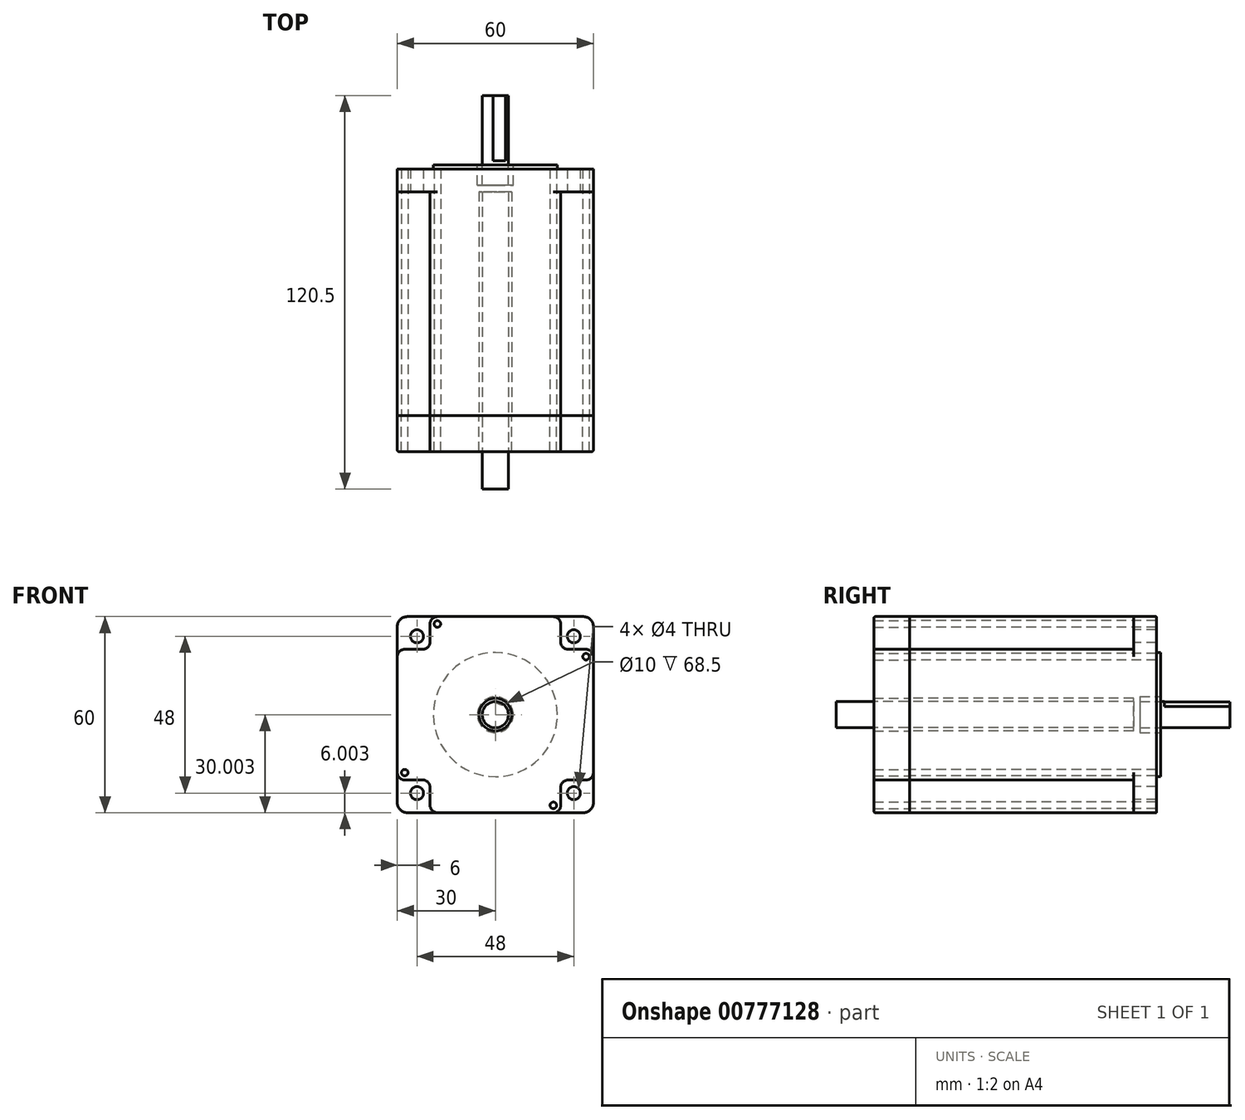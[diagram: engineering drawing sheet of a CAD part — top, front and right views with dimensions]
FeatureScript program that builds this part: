
annotation { "Feature Type Name" : "Feature", "Feature Type Description" : "" }
export const myFeature = defineFeature(function(context is Context, id is Id, definition is map)
    precondition{}
    {
        {
            var Q0;
            Q0=qCreatedBy(makeId("Front.planeOp"),FACE);
            var sketch = newSketch(context, id + "F0", { "sketchPlane" : qUnion([Q0])});
            skLineSegment(sketch, "E0.bottom", {"start": v(-39, 29.62) * mm, "end": v(-3.5, 29.62) * mm});
            skLineSegment(sketch, "E0.top", {"start": v(-39, -30.38) * mm, "end": v(-3.5, -30.38) * mm});
            skLineSegment(sketch, "E0.left", {"start": v(-51.25, 17.37) * mm, "end": v(-51.25, -18.13) * mm});
            skLineSegment(sketch, "E0.right", {"start": v(8.75, 17.37) * mm, "end": v(8.75, -18.13) * mm});
            skLineSegment(sketch, "E1.bottom", {"start": v(-49, 29.62) * mm, "end": v(-41.25, 29.62) * mm});
            skLineSegment(sketch, "E1.top", {"start": v(-49, 19.62) * mm, "end": v(-43.5, 19.62) * mm});
            skLineSegment(sketch, "E1.left", {"start": v(-51.25, 27.37) * mm, "end": v(-51.25, 19.62) * mm});
            skLineSegment(sketch, "E1.right", {"start": v(-41.25, 27.37) * mm, "end": v(-41.25, 21.87) * mm});
            skLineSegment(sketch, "E2.bottom", {"start": v(6.5, 19.62) * mm, "end": v(1, 19.62) * mm});
            skLineSegment(sketch, "E2.top", {"start": v(6.5, 29.62) * mm, "end": v(0, 29.62) * mm});
            skLineSegment(sketch, "E2.left", {"start": v(8.75, 19.62) * mm, "end": v(8.75, 27.37) * mm});
            skLineSegment(sketch, "E2.right", {"start": v(-1.25, 21.87) * mm, "end": v(-1.25, 27.37) * mm});
            skLineSegment(sketch, "E3.bottom", {"start": v(-43.5, -20.38) * mm, "end": v(-49, -20.38) * mm});
            skLineSegment(sketch, "E3.top", {"start": v(-41.25, -30.38) * mm, "end": v(-49, -30.38) * mm});
            skLineSegment(sketch, "E3.left", {"start": v(-41.25, -22.63) * mm, "end": v(-41.25, -28.13) * mm});
            skLineSegment(sketch, "E3.right", {"start": v(-51.25, -20.38) * mm, "end": v(-51.25, -28.13) * mm});
            skLineSegment(sketch, "E4.bottom", {"start": v(1, -20.38) * mm, "end": v(6.5, -20.38) * mm});
            skLineSegment(sketch, "E4.top", {"start": v(-1.25, -30.38) * mm, "end": v(6.5, -30.38) * mm});
            skLineSegment(sketch, "E4.left", {"start": v(-1.25, -22.63) * mm, "end": v(-1.25, -28.13) * mm});
            skLineSegment(sketch, "E4.right", {"start": v(8.75, -20.38) * mm, "end": v(8.75, -28.13) * mm});
            skArc(sketch, "E5.filletArc", {"start": v(-1.25, 27.37) * mm, "mid": v(-1.9, 28.96) * mm, "end": v(-3.5, 29.62) * mm});
            skPoint(sketch, "E6.visualSharp", {"position": v(-1.25, 19.62) * mm});
            skArc(sketch, "E6.filletArc", {"start": v(-1.25, 21.87) * mm, "mid": v(-0.6, 20.28) * mm, "end": v(1, 19.62) * mm});
            skPoint(sketch, "E7.newPointA", {"position": v(8.75, 19.62) * mm});
            skArc(sketch, "E7.filletArc", {"start": v(8.75, 17.37) * mm, "mid": v(8.1, 18.96) * mm, "end": v(6.5, 19.62) * mm});
            skPoint(sketch, "E8.visualSharp", {"position": v(-1.25, -20.38) * mm});
            skArc(sketch, "E8.filletArc", {"start": v(1, -20.38) * mm, "mid": v(-0.6, -21.04) * mm, "end": v(-1.25, -22.63) * mm});
            skArc(sketch, "E9.filletArc", {"start": v(6.5, -20.38) * mm, "mid": v(8.1, -19.72) * mm, "end": v(8.75, -18.13) * mm});
            skArc(sketch, "E10.filletArc", {"start": v(-3.5, -30.38) * mm, "mid": v(-1.9, -29.72) * mm, "end": v(-1.25, -28.13) * mm});
            skArc(sketch, "E11.filletArc", {"start": v(-41.25, -28.13) * mm, "mid": v(-40.6, -29.72) * mm, "end": v(-39, -30.38) * mm});
            skPoint(sketch, "E12.visualSharp", {"position": v(-41.25, -20.38) * mm});
            skArc(sketch, "E12.filletArc", {"start": v(-41.25, -22.63) * mm, "mid": v(-41.9, -21.04) * mm, "end": v(-43.5, -20.38) * mm});
            skPoint(sketch, "E13.newPointA", {"position": v(-51.25, -30.38) * mm});
            skArc(sketch, "E13.filletArc", {"start": v(-51.25, -18.13) * mm, "mid": v(-50.6, -19.72) * mm, "end": v(-49, -20.38) * mm});
            skPoint(sketch, "E14.newPointA", {"position": v(-51.25, 19.62) * mm});
            skPoint(sketch, "E14.newPointB", {"position": v(-51.25, 29.62) * mm});
            skArc(sketch, "E14.filletArc", {"start": v(-49, 19.62) * mm, "mid": v(-50.6, 18.96) * mm, "end": v(-51.25, 17.37) * mm});
            skPoint(sketch, "E15.visualSharp", {"position": v(-41.25, 19.62) * mm});
            skArc(sketch, "E15.filletArc", {"start": v(-43.5, 19.62) * mm, "mid": v(-41.9, 20.28) * mm, "end": v(-41.25, 21.87) * mm});
            skPoint(sketch, "E16.newPointB", {"position": v(-41.25, 29.62) * mm});
            skArc(sketch, "E16.filletArc", {"start": v(-39, 29.62) * mm, "mid": v(-40.6, 28.96) * mm, "end": v(-41.25, 27.37) * mm});
            skArc(sketch, "E17.filletArc", {"start": v(-49, 29.62) * mm, "mid": v(-50.6, 28.96) * mm, "end": v(-51.25, 27.37) * mm});
            skPoint(sketch, "E18.visualSharp", {"position": v(8.75, 29.62) * mm});
            skArc(sketch, "E18.filletArc", {"start": v(8.75, 27.37) * mm, "mid": v(8.1, 28.96) * mm, "end": v(6.5, 29.62) * mm});
            skPoint(sketch, "E19.visualSharp", {"position": v(8.75, -30.38) * mm});
            skArc(sketch, "E19.filletArc", {"start": v(6.5, -30.38) * mm, "mid": v(8.1, -29.72) * mm, "end": v(8.75, -28.13) * mm});
            skArc(sketch, "E20.filletArc", {"start": v(-51.25, -28.13) * mm, "mid": v(-50.6, -29.72) * mm, "end": v(-49, -30.38) * mm});
            skLineSegment(sketch, "E21", {"start": v(-51.25, 19.62) * mm, "end": v(-51.25, 17.37) * mm});
            skLineSegment(sketch, "E22", {"start": v(-51.25, -18.13) * mm, "end": v(-51.25, -20.38) * mm});
            skLineSegment(sketch, "E23", {"start": v(-41.25, -30.38) * mm, "end": v(-39, -30.38) * mm});
            skLineSegment(sketch, "E24", {"start": v(-3.6, -30.34) * mm, "end": v(-1.25, -30.38) * mm});
            skLineSegment(sketch, "E25", {"start": v(8.75, -20.38) * mm, "end": v(8.75, -18.13) * mm});
            skLineSegment(sketch, "E26", {"start": v(8.75, 17.37) * mm, "end": v(8.75, 19.62) * mm});
            skLineSegment(sketch, "E27", {"start": v(0, 29.62) * mm, "end": v(-3.5, 29.62) * mm});
            skLineSegment(sketch, "E28", {"start": v(-39, 29.62) * mm, "end": v(-41.25, 29.62) * mm});
            skCircle(sketch, "E29", {"center": v(-39, 27.37) * mm, "radius": 1 * mm});
            skCircle(sketch, "E30", {"center": v(6.5, 17.37) * mm, "radius": 1 * mm});
            skCircle(sketch, "E31", {"center": v(-3.5, -28.13) * mm, "radius": 1 * mm});
            skCircle(sketch, "E32", {"center": v(-49, -18.13) * mm, "radius": 1 * mm});
            skCircle(sketch, "E33", {"center": v(-21.25, -0.38) * mm, "radius": 5 * mm});
            skPoint(sketch, "E33.centerSnap0", {"position": v(-21.25, 29.62) * mm});
            skPoint(sketch, "E33.centerSnap1", {"position": v(-51.25, -0.38) * mm});
            skCircle(sketch, "E34", {"center": v(-21.25, -0.38) * mm, "radius": 4 * mm});
            skSolve(sketch);
        }
        {
            var Q0;
            Q0=makeQuery(id+"F0.imprint","IMPRINT",FACE,{"disambiguationData":[TD([[makeQuery(id+"F0.imprint","IMPRINT",EDGE,{"derivedFrom":sQuery(id+"F0.wireOp",EDGE,"E0.bottom")}),-1.0]])]});
            extrude(context, id + "F1", {"entities" : qUnion([Q0]), "depth" : 11 * mm, "offsetDistance" : 25 * mm});
        }
        {
            var Q0;
            Q0=makeQuery(id+"F1.opExtrude","CAP_EDGE",EDGE,{"disambiguationData":[OSD([sQuery(id+"F0.wireOp",EDGE,"E0.left")])],"isStart":false});
            fillet(context, id + "F2", {"entities" : qUnion([Q0]), "radius" : .5 * mm, "tangentPropagation" : true, "allowEdgeOverflow" : false});
        }
        {
            var Q0;
            Q0=makeQuery(id+"F1.opExtrude","CAP_FACE",FACE,{"disambiguationData":[OSD([sQuery(id+"F0.wireOp",EDGE,"E0.bottom"),sQuery(id+"F0.wireOp",EDGE,"E0.top"),sQuery(id+"F0.wireOp",EDGE,"E0.left"),sQuery(id+"F0.wireOp",EDGE,"E0.right"),sQuery(id+"F0.wireOp",EDGE,"E1.top"),sQuery(id+"F0.wireOp",EDGE,"E1.right"),sQuery(id+"F0.wireOp",EDGE,"E2.bottom"),sQuery(id+"F0.wireOp",EDGE,"E2.right"),sQuery(id+"F0.wireOp",EDGE,"E3.bottom"),sQuery(id+"F0.wireOp",EDGE,"E3.left"),sQuery(id+"F0.wireOp",EDGE,"E4.bottom"),sQuery(id+"F0.wireOp",EDGE,"E4.left"),sQuery(id+"F0.wireOp",EDGE,"E5.filletArc"),sQuery(id+"F0.wireOp",EDGE,"E6.filletArc"),sQuery(id+"F0.wireOp",EDGE,"E7.filletArc"),sQuery(id+"F0.wireOp",EDGE,"E8.filletArc"),sQuery(id+"F0.wireOp",EDGE,"E9.filletArc"),sQuery(id+"F0.wireOp",EDGE,"E10.filletArc"),sQuery(id+"F0.wireOp",EDGE,"E11.filletArc"),sQuery(id+"F0.wireOp",EDGE,"E12.filletArc"),sQuery(id+"F0.wireOp",EDGE,"E13.filletArc"),sQuery(id+"F0.wireOp",EDGE,"E14.filletArc"),sQuery(id+"F0.wireOp",EDGE,"E15.filletArc"),sQuery(id+"F0.wireOp",EDGE,"E16.filletArc"),sQuery(id+"F0.wireOp",EDGE,"E29"),sQuery(id+"F0.wireOp",EDGE,"E30"),sQuery(id+"F0.wireOp",EDGE,"E31"),sQuery(id+"F0.wireOp",EDGE,"E32"),sQuery(id+"F0.wireOp",EDGE,"E33")])],"isStart":true});
            var sketch = newSketch(context, id + "F3", { "sketchPlane" : qUnion([Q0])});
            skSolve(sketch);
        }
        {
            var Q0;
            Q0 = qSketchRegion(id + "F3", true);
            var Q1;
            Q1=makeQuery(id+"F3.imprint","IMPRINT",FACE,{"disambiguationData":[TD([[makeQuery(id+"F3.imprint","IMPRINT",EDGE,{"derivedFrom":makeQuery(id+"F1.opExtrude","CAP_EDGE",EDGE,{"disambiguationData":[OSD([sQuery(id+"F0.wireOp",EDGE,"E0.bottom")])],"isStart":true})}),1.0]])]});
            extrude(context, id + "F4", {"entities" : qUnion([Q0, Q1]), "depth" : 65.5 * mm, "offsetDistance" : 25 * mm});
        }
        {
            var Q0;
            Q0=makeQuery(id+"F4.opExtrude","SWEPT_FACE",FACE,{"disambiguationData":[OSD([sQuery(id+"F0.wireOp",EDGE,"E1.right")])]});
            var sketch = newSketch(context, id + "F5", { "sketchPlane" : qUnion([Q0])});
            skSolve(sketch);
        }
        {
            var Q0;
            Q0 = qSketchRegion(id + "F5", true);
            var Q1;
            Q1=makeQuery(id+"F4.opExtrude","CAP_FACE",FACE,{"disambiguationData":[OSD([sQuery(id+"F0.wireOp",EDGE,"E0.bottom"),sQuery(id+"F0.wireOp",EDGE,"E0.top"),sQuery(id+"F0.wireOp",EDGE,"E0.left"),sQuery(id+"F0.wireOp",EDGE,"E0.right"),sQuery(id+"F0.wireOp",EDGE,"E1.top"),sQuery(id+"F0.wireOp",EDGE,"E1.right"),sQuery(id+"F0.wireOp",EDGE,"E2.bottom"),sQuery(id+"F0.wireOp",EDGE,"E2.right"),sQuery(id+"F0.wireOp",EDGE,"E3.bottom"),sQuery(id+"F0.wireOp",EDGE,"E3.left"),sQuery(id+"F0.wireOp",EDGE,"E4.bottom"),sQuery(id+"F0.wireOp",EDGE,"E4.left"),sQuery(id+"F0.wireOp",EDGE,"E5.filletArc"),sQuery(id+"F0.wireOp",EDGE,"E6.filletArc"),sQuery(id+"F0.wireOp",EDGE,"E7.filletArc"),sQuery(id+"F0.wireOp",EDGE,"E8.filletArc"),sQuery(id+"F0.wireOp",EDGE,"E9.filletArc"),sQuery(id+"F0.wireOp",EDGE,"E10.filletArc"),sQuery(id+"F0.wireOp",EDGE,"E11.filletArc"),sQuery(id+"F0.wireOp",EDGE,"E12.filletArc"),sQuery(id+"F0.wireOp",EDGE,"E13.filletArc"),sQuery(id+"F0.wireOp",EDGE,"E14.filletArc"),sQuery(id+"F0.wireOp",EDGE,"E15.filletArc"),sQuery(id+"F0.wireOp",EDGE,"E16.filletArc"),sQuery(id+"F0.wireOp",EDGE,"E29"),sQuery(id+"F0.wireOp",EDGE,"E30"),sQuery(id+"F0.wireOp",EDGE,"E31"),sQuery(id+"F0.wireOp",EDGE,"E32"),sQuery(id+"F0.wireOp",EDGE,"E33")])],"isStart":false});
            extrude(context, id + "F6", {"entities" : qUnion([Q0, Q1]), "operationType" : NewBodyOperationType.ADD, "depth" : 3 * mm, "offsetDistance" : 25 * mm});
        }
        {
            var Q0;
            Q0=makeQuery(id+"F6.opExtrude","CAP_FACE",FACE,{"disambiguationData":[OSD([sQuery(id+"F0.wireOp",EDGE,"E0.bottom"),sQuery(id+"F0.wireOp",EDGE,"E0.top"),sQuery(id+"F0.wireOp",EDGE,"E0.left"),sQuery(id+"F0.wireOp",EDGE,"E0.right"),sQuery(id+"F0.wireOp",EDGE,"E1.top"),sQuery(id+"F0.wireOp",EDGE,"E1.right"),sQuery(id+"F0.wireOp",EDGE,"E2.bottom"),sQuery(id+"F0.wireOp",EDGE,"E2.right"),sQuery(id+"F0.wireOp",EDGE,"E3.bottom"),sQuery(id+"F0.wireOp",EDGE,"E3.left"),sQuery(id+"F0.wireOp",EDGE,"E4.bottom"),sQuery(id+"F0.wireOp",EDGE,"E4.left"),sQuery(id+"F0.wireOp",EDGE,"E5.filletArc"),sQuery(id+"F0.wireOp",EDGE,"E6.filletArc"),sQuery(id+"F0.wireOp",EDGE,"E7.filletArc"),sQuery(id+"F0.wireOp",EDGE,"E8.filletArc"),sQuery(id+"F0.wireOp",EDGE,"E9.filletArc"),sQuery(id+"F0.wireOp",EDGE,"E10.filletArc"),sQuery(id+"F0.wireOp",EDGE,"E11.filletArc"),sQuery(id+"F0.wireOp",EDGE,"E12.filletArc"),sQuery(id+"F0.wireOp",EDGE,"E13.filletArc"),sQuery(id+"F0.wireOp",EDGE,"E14.filletArc"),sQuery(id+"F0.wireOp",EDGE,"E15.filletArc"),sQuery(id+"F0.wireOp",EDGE,"E16.filletArc"),sQuery(id+"F0.wireOp",EDGE,"E29"),sQuery(id+"F0.wireOp",EDGE,"E30"),sQuery(id+"F0.wireOp",EDGE,"E31"),sQuery(id+"F0.wireOp",EDGE,"E32"),sQuery(id+"F0.wireOp",EDGE,"E33")])],"isStart":false});
            var sketch = newSketch(context, id + "F7", { "sketchPlane" : qUnion([Q0])});
            skLineSegment(sketch, "E35.bottom", {"start": v(-5.75, 29.62) * mm, "end": v(48.25, 29.62) * mm});
            skLineSegment(sketch, "E35.top", {"start": v(-5.75, -30.38) * mm, "end": v(48.25, -30.38) * mm});
            skLineSegment(sketch, "E35.left", {"start": v(-8.75, 26.62) * mm, "end": v(-8.75, -27.38) * mm});
            skLineSegment(sketch, "E35.right", {"start": v(51.25, 26.62) * mm, "end": v(51.25, -27.38) * mm});
            skPoint(sketch, "E36.visualSharp", {"position": v(-8.75, 29.62) * mm});
            skArc(sketch, "E36.filletArc", {"start": v(-5.75, 29.62) * mm, "mid": v(-7.87, 28.74) * mm, "end": v(-8.75, 26.62) * mm});
            skPoint(sketch, "E37.visualSharp", {"position": v(51.25, 29.62) * mm});
            skArc(sketch, "E37.filletArc", {"start": v(51.25, 26.62) * mm, "mid": v(50.37, 28.74) * mm, "end": v(48.25, 29.62) * mm});
            skPoint(sketch, "E38.visualSharp", {"position": v(-8.75, -30.38) * mm});
            skArc(sketch, "E38.filletArc", {"start": v(-8.75, -27.38) * mm, "mid": v(-7.87, -29.5) * mm, "end": v(-5.75, -30.38) * mm});
            skPoint(sketch, "E39.visualSharp", {"position": v(51.25, -30.38) * mm});
            skArc(sketch, "E39.filletArc", {"start": v(48.25, -30.38) * mm, "mid": v(50.37, -29.5) * mm, "end": v(51.25, -27.38) * mm});
            skCircle(sketch, "E40", {"center": v(-2.75, 23.62) * mm, "radius": 2 * mm});
            skCircle(sketch, "E41", {"center": v(-2.75, -24.38) * mm, "radius": 2 * mm});
            skCircle(sketch, "E42", {"center": v(45.25, -24.38) * mm, "radius": 2 * mm});
            skCircle(sketch, "E43", {"center": v(45.25, 23.62) * mm, "radius": 2 * mm});
            skSolve(sketch);
        }
        {
            var Q0;
            Q0 = qSketchRegion(id + "F7", true);
            extrude(context, id + "F8", {"entities" : qUnion([Q0]), "operationType" : NewBodyOperationType.ADD, "depth" : 7 * mm, "offsetDistance" : 25 * mm});
        }
        {
            var Q0;
            Q0=makeQuery(id+"F8.opExtrude","CAP_FACE",FACE,{"disambiguationData":[OSD([sQuery(id+"F7.wireOp",EDGE,"E35.bottom"),sQuery(id+"F7.wireOp",EDGE,"E35.top"),sQuery(id+"F7.wireOp",EDGE,"E35.left"),sQuery(id+"F7.wireOp",EDGE,"E35.right"),sQuery(id+"F7.wireOp",EDGE,"E36.filletArc"),sQuery(id+"F7.wireOp",EDGE,"E37.filletArc"),sQuery(id+"F7.wireOp",EDGE,"E38.filletArc"),sQuery(id+"F7.wireOp",EDGE,"E39.filletArc"),sQuery(id+"F7.wireOp",EDGE,"E40"),sQuery(id+"F7.wireOp",EDGE,"E41"),sQuery(id+"F7.wireOp",EDGE,"E42"),sQuery(id+"F7.wireOp",EDGE,"E43")])],"isStart":false});
            var sketch = newSketch(context, id + "F9", { "sketchPlane" : qUnion([Q0])});
            skCircle(sketch, "E44", {"center": v(21.25, -0.38) * mm, "radius": 19 * mm});
            skPoint(sketch, "E44.centerSnap0", {"position": v(-8.75, -0.38) * mm});
            skPoint(sketch, "E44.centerSnap1", {"position": v(21.25, 29.62) * mm});
            skCircle(sketch, "E45", {"center": v(21.25, -0.38) * mm, "radius": 5.5 * mm});
            skCircle(sketch, "E46", {"center": v(21.25, -0.38) * mm, "radius": 4 * mm});
            skSolve(sketch);
        }
        {
            var Q0;
            Q0=makeQuery(id+"F9.imprint","IMPRINT",FACE,{"disambiguationData":[TD([[makeQuery(id+"F9.imprint","IMPRINT",EDGE,{"derivedFrom":sQuery(id+"F9.wireOp",EDGE,"E45")}),1.0]])]});
            extrude(context, id + "F10", {"entities" : qUnion([Q0]), "operationType" : NewBodyOperationType.REMOVE, "oppositeDirection" : true, "depth" : 5 * mm, "offsetDistance" : 25 * mm});
        }
        {
            var Q0;
            Q0=makeQuery(id+"F10.boolean.opBoolean","SPLIT",FACE,{"disambiguationData":[TD([makeQuery(id+"F10.opExtrude","SWEPT_FACE",FACE,{"disambiguationData":[OSD([sQuery(id+"F9.wireOp",EDGE,"E46")])]})])],"derivedFrom":makeQuery(id+"F8.opExtrude","CAP_FACE",FACE,{"disambiguationData":[OSD([sQuery(id+"F7.wireOp",EDGE,"E35.bottom"),sQuery(id+"F7.wireOp",EDGE,"E35.top"),sQuery(id+"F7.wireOp",EDGE,"E35.left"),sQuery(id+"F7.wireOp",EDGE,"E35.right"),sQuery(id+"F7.wireOp",EDGE,"E36.filletArc"),sQuery(id+"F7.wireOp",EDGE,"E37.filletArc"),sQuery(id+"F7.wireOp",EDGE,"E38.filletArc"),sQuery(id+"F7.wireOp",EDGE,"E39.filletArc"),sQuery(id+"F7.wireOp",EDGE,"E40"),sQuery(id+"F7.wireOp",EDGE,"E41"),sQuery(id+"F7.wireOp",EDGE,"E42"),sQuery(id+"F7.wireOp",EDGE,"E43")])],"isStart":false})});
            extrude(context, id + "F11", {"entities" : qUnion([Q0]), "operationType" : NewBodyOperationType.ADD, "depth" : 22.5 * mm, "offsetDistance" : 25 * mm, "hasSecondDirection" : true, "secondDirectionOppositeDirection" : true, "secondDirectionDepth" : 98 * mm});
        }
        {
            var Q0;
            Q0=makeQuery(id+"F11.opExtrude","CAP_FACE",FACE,{"disambiguationData":[OSD([sQuery(id+"F7.wireOp",EDGE,"E35.bottom"),sQuery(id+"F7.wireOp",EDGE,"E35.top"),sQuery(id+"F7.wireOp",EDGE,"E35.left"),sQuery(id+"F7.wireOp",EDGE,"E35.right"),sQuery(id+"F7.wireOp",EDGE,"E36.filletArc"),sQuery(id+"F7.wireOp",EDGE,"E37.filletArc"),sQuery(id+"F7.wireOp",EDGE,"E38.filletArc"),sQuery(id+"F7.wireOp",EDGE,"E39.filletArc"),sQuery(id+"F7.wireOp",EDGE,"E40"),sQuery(id+"F7.wireOp",EDGE,"E41"),sQuery(id+"F7.wireOp",EDGE,"E42"),sQuery(id+"F7.wireOp",EDGE,"E43")])],"isStart":false});
            var sketch = newSketch(context, id + "F12", { "sketchPlane" : qUnion([Q0])});
            skLineSegment(sketch, "E47", {"start": v(21.9, 3.57) * mm, "end": v(18.16, 2.16) * mm});
            skSolve(sketch);
        }
        {
            var Q0;
            {var subQ0=sQuery(id+"F12.wireOp",EDGE,"E47");Q0=makeQuery(id+"F12.imprint","IMPRINT",FACE,{"disambiguationData":[TD([[makeQuery(id+"F12.imprint","IMPRINT",EDGE,{"derivedFrom":subQ0}),-1.0]])]});}
            extrude(context, id + "F13", {"entities" : qUnion([Q0]), "operationType" : NewBodyOperationType.REMOVE, "oppositeDirection" : true, "depth" : 20 * mm, "offsetDistance" : 25 * mm});
        }
        {
            var Q0;
            Q0 = qSketchRegion(id + "F9", true);
            extrude(context, id + "F14", {"entities" : qUnion([Q0]), "operationType" : NewBodyOperationType.ADD, "depth" : 1.25 * mm, "offsetDistance" : 25 * mm});
        }
        {
            var Q0;
            Q0=makeQuery(id+"F8.opExtrude","CAP_EDGE",EDGE,{"disambiguationData":[OSD([sQuery(id+"F7.wireOp",EDGE,"E35.right")])],"isStart":false});
            fillet(context, id + "F15", {"entities" : qUnion([Q0]), "radius" : .1 * mm, "tangentPropagation" : true, "allowEdgeOverflow" : false});
        }
        {
            var Q0;
            Q0=makeQuery(id+"F0.imprint","IMPRINT",FACE,{"disambiguationData":[TD([[makeQuery(id+"F0.imprint","IMPRINT",EDGE,{"derivedFrom":sQuery(id+"F0.wireOp",EDGE,"E30")}),1.0]])]});
            var Q1;
            Q1=makeQuery(id+"F0.imprint","IMPRINT",FACE,{"disambiguationData":[TD([[makeQuery(id+"F0.imprint","IMPRINT",EDGE,{"derivedFrom":sQuery(id+"F0.wireOp",EDGE,"E32")}),1.0]])]});
            var Q2;
            Q2=makeQuery(id+"F0.imprint","IMPRINT",FACE,{"disambiguationData":[TD([[makeQuery(id+"F0.imprint","IMPRINT",EDGE,{"derivedFrom":sQuery(id+"F0.wireOp",EDGE,"E31")}),1.0]])]});
            var Q3;
            Q3=makeQuery(id+"F0.imprint","IMPRINT",FACE,{"disambiguationData":[TD([[makeQuery(id+"F0.imprint","IMPRINT",EDGE,{"derivedFrom":sQuery(id+"F0.wireOp",EDGE,"E29")}),1.0]])]});
            var Q4;
            Q4=makeQuery(id+"F14.opExtrude","CAP_FACE",FACE,{"disambiguationData":[OSD([sQuery(id+"F9.wireOp",EDGE,"E44"),sQuery(id+"F9.wireOp",EDGE,"E45")])],"isStart":false});
            extrude(context, id + "F16", {"entities" : qUnion([Q0, Q1, Q2, Q3]), "operationType" : NewBodyOperationType.REMOVE, "endBound" : BoundingType.UP_TO_SURFACE, "oppositeDirection" : true, "depth" : 25 * mm, "endBoundEntityFace" : qUnion([Q4]), "offsetDistance" : 25 * mm});
        }
    });
